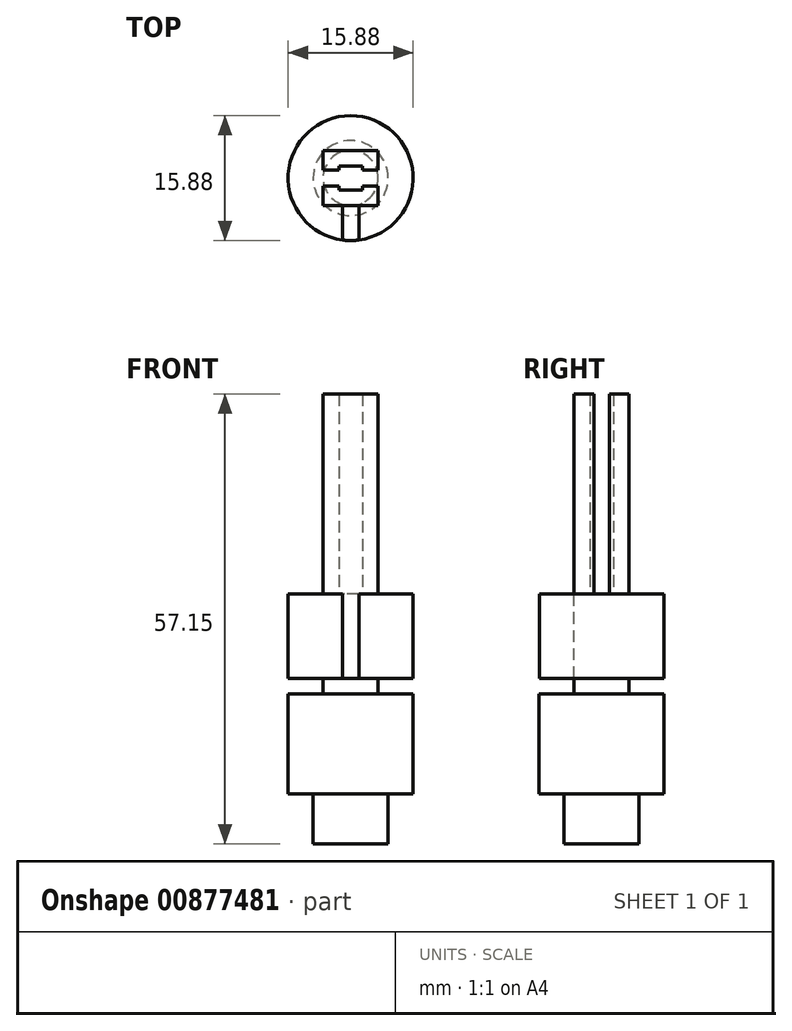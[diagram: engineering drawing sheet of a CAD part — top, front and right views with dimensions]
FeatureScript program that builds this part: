
annotation { "Feature Type Name" : "Feature", "Feature Type Description" : "" }
export const myFeature = defineFeature(function(context is Context, id is Id, definition is map)
    precondition{}
    {
        {
            var Q0;
            Q0=qCreatedBy(makeId("Top.planeOp"),FACE);
            var sketch = newSketch(context, id + "F0", { "sketchPlane" : qUnion([Q0])});
            skCircle(sketch, "E0", {"center": v(0, 0) * mm, "radius": 7.94 * mm});
            skSolve(sketch);
        }
        {
            var Q0;
            Q0 = qSketchRegion(id + "F0", true);
            extrude(context, id + "F1", {"entities" : qUnion([Q0]), "depth" : 25.4 * mm, "offsetDistance" : 25.4 * mm});
        }
        {
            var Q0;
            Q0=qCreatedBy(makeId("Top.planeOp"),FACE);
            var sketch = newSketch(context, id + "F2", { "sketchPlane" : qUnion([Q0])});
            skCircle(sketch, "E1", {"center": v(0, 0) * mm, "radius": 4.76 * mm});
            skSolve(sketch);
        }
        {
            var Q0;
            Q0 = qSketchRegion(id + "F2", true);
            extrude(context, id + "F3", {"entities" : qUnion([Q0]), "operationType" : NewBodyOperationType.ADD, "oppositeDirection" : true, "depth" : 6.35 * mm, "offsetDistance" : 25.4 * mm});
        }
        {
            var Q0;
            Q0=makeQuery(id+"F1.opExtrude","CAP_FACE",FACE,{"disambiguationData":[OSD([sQuery(id+"F0.wireOp",EDGE,"E0")])],"isStart":false});
            var sketch = newSketch(context, id + "F4", { "sketchPlane" : qUnion([Q0])});
            skLineSegment(sketch, "E2.bottom", {"start": v(3.5, 3.5) * mm, "end": v(-3.5, 3.5) * mm});
            skLineSegment(sketch, "E2.top", {"start": v(3.5, -3.5) * mm, "end": v(-3.5, -3.5) * mm});
            skLineSegment(sketch, "E2.left", {"start": v(3.5, 3.5) * mm, "end": v(3.5, -3.5) * mm});
            skLineSegment(sketch, "E2.right", {"start": v(-3.5, 3.5) * mm, "end": v(-3.5, -3.5) * mm});
            skPoint(sketch, "E2.middle", {"position": v(0, 0) * mm});
            skSolve(sketch);
        }
        {
            var Q0;
            Q0 = qSketchRegion(id + "F4", true);
            extrude(context, id + "F5", {"entities" : qUnion([Q0]), "operationType" : NewBodyOperationType.ADD, "depth" : 25.4 * mm, "offsetDistance" : 25.4 * mm});
        }
        {
            var Q0;
            Q0=makeQuery(id+"F1.opExtrude","CAP_FACE",FACE,{"disambiguationData":[OSD([sQuery(id+"F0.wireOp",EDGE,"E0")])],"isStart":false});
            var sketch = newSketch(context, id + "F6", { "sketchPlane" : qUnion([Q0])});
            skLineSegment(sketch, "E3.bottom", {"start": v(1.5, 1.5) * mm, "end": v(-1.5, 1.5) * mm});
            skLineSegment(sketch, "E3.top", {"start": v(1.5, -1.5) * mm, "end": v(-1.5, -1.5) * mm});
            skLineSegment(sketch, "E3.left", {"start": v(1.5, 1.5) * mm, "end": v(1.5, -1.5) * mm});
            skLineSegment(sketch, "E3.right", {"start": v(-1.5, 1.5) * mm, "end": v(-1.5, -1.5) * mm});
            skPoint(sketch, "E3.middle", {"position": v(0, 0) * mm});
            skSolve(sketch);
        }
        {
            var Q0;
            Q0 = qSketchRegion(id + "F6", true);
            extrude(context, id + "F7", {"entities" : qUnion([Q0]), "depth" : 25.4 * mm, "offsetDistance" : 25.4 * mm});
        }
        {
            var Q0;
            Q0=makeQuery(id+"F7.opExtrude","SWEPT_BODY",BODY,{"disambiguationData":[OSD([sQuery(id+"F6.wireOp",EDGE,"E3.bottom"),sQuery(id+"F6.wireOp",EDGE,"E3.top"),sQuery(id+"F6.wireOp",EDGE,"E3.left"),sQuery(id+"F6.wireOp",EDGE,"E3.right")])]});
            var Q1;
            Q1=makeQuery(id+"F1.opExtrude","SWEPT_BODY",BODY,{"disambiguationData":[OSD([sQuery(id+"F0.wireOp",EDGE,"E0")])]});
            booleanBodies(context, id + "F8", {"operationType" : BooleanOperationType.SUBTRACTION, "tools" : qUnion([Q0]), "targets" : qUnion([Q1])});
        }
        {
            var Q0;
            Q0=makeQuery(id+"F1.opExtrude","CAP_FACE",FACE,{"disambiguationData":[OSD([sQuery(id+"F0.wireOp",EDGE,"E0")])],"isStart":false});
            var sketch = newSketch(context, id + "F9", { "sketchPlane" : qUnion([Q0])});
            skLineSegment(sketch, "E4.bottom", {"start": v(7.87, 1) * mm, "end": v(-7.87, 1) * mm});
            skLineSegment(sketch, "E4.top", {"start": v(7.87, -1) * mm, "end": v(-7.87, -1) * mm});
            skLineSegment(sketch, "E4.left", {"start": v(7.87, 1) * mm, "end": v(7.87, -1) * mm});
            skLineSegment(sketch, "E4.right", {"start": v(-7.87, 1) * mm, "end": v(-7.87, -1) * mm});
            skPoint(sketch, "E4.middle", {"position": v(0, 0) * mm});
            skSolve(sketch);
        }
        {
            var Q0;
            Q0 = qSketchRegion(id + "F9", true);
            extrude(context, id + "F10", {"entities" : qUnion([Q0]), "depth" : 25.4 * mm, "offsetDistance" : 25.4 * mm});
        }
        {
            var Q0;
            Q0=makeQuery(id+"F10.opExtrude","SWEPT_BODY",BODY,{"disambiguationData":[OSD([sQuery(id+"F9.wireOp",EDGE,"E4.bottom"),sQuery(id+"F9.wireOp",EDGE,"E4.top"),sQuery(id+"F9.wireOp",EDGE,"E4.left"),sQuery(id+"F9.wireOp",EDGE,"E4.right")])]});
            var Q1;
            Q1=makeQuery(id+"F1.opExtrude","SWEPT_BODY",BODY,{"disambiguationData":[OSD([sQuery(id+"F0.wireOp",EDGE,"E0")])]});
            booleanBodies(context, id + "F11", {"operationType" : BooleanOperationType.SUBTRACTION, "tools" : qUnion([Q0]), "targets" : qUnion([Q1])});
        }
        {
            var Q0;
            Q0=makeQuery(id+"F5.opExtrude","SWEPT_FACE",FACE,{"disambiguationData":[OSD([sQuery(id+"F4.wireOp",EDGE,"E2.top")])]});
            var sketch = newSketch(context, id + "F12", { "sketchPlane" : qUnion([Q0])});
            skLineSegment(sketch, "E5.bottom", {"start": v(1.04, 12.7) * mm, "end": v(-1.04, 12.7) * mm});
            skLineSegment(sketch, "E5.top", {"start": v(1.04, 25.4) * mm, "end": v(-1.04, 25.4) * mm});
            skLineSegment(sketch, "E5.left", {"start": v(1.04, 12.7) * mm, "end": v(1.04, 25.4) * mm});
            skLineSegment(sketch, "E5.right", {"start": v(-1.04, 12.7) * mm, "end": v(-1.04, 25.4) * mm});
            skPoint(sketch, "E5.middle", {"position": v(0, 19.05) * mm});
            skSolve(sketch);
        }
        {
            var Q0;
            Q0 = qSketchRegion(id + "F12", true);
            extrude(context, id + "F13", {"entities" : qUnion([Q0]), "depth" : 25.4 * mm, "offsetDistance" : 25.4 * mm});
        }
        {
            var Q0;
            Q0=makeQuery(id+"F13.opExtrude","SWEPT_BODY",BODY,{"disambiguationData":[OSD([sQuery(id+"F12.wireOp",EDGE,"E5.bottom"),sQuery(id+"F12.wireOp",EDGE,"E5.top"),sQuery(id+"F12.wireOp",EDGE,"E5.left"),sQuery(id+"F12.wireOp",EDGE,"E5.right")])]});
            var Q1;
            Q1=makeQuery(id+"F1.opExtrude","SWEPT_BODY",BODY,{"disambiguationData":[OSD([sQuery(id+"F0.wireOp",EDGE,"E0")])]});
            booleanBodies(context, id + "F14", {"operationType" : BooleanOperationType.SUBTRACTION, "tools" : qUnion([Q0]), "targets" : qUnion([Q1])});
        }
        {
            var Q0;
            Q0=makeQuery(id+"F14.opBoolean","COPY",FACE,{"derivedFrom":makeQuery(id+"F13.opExtrude","SWEPT_FACE",FACE,{"disambiguationData":[OSD([sQuery(id+"F12.wireOp",EDGE,"E5.bottom")])]})});
            var sketch = newSketch(context, id + "F15", { "sketchPlane" : qUnion([Q0])});
            skCircle(sketch, "E6", {"center": v(0, 0) * mm, "radius": 3.5 * mm});
            skCircle(sketch, "E7", {"center": v(0, 0) * mm, "radius": 7.94 * mm});
            skSolve(sketch);
        }
        {
            var Q0;
            Q0 = qSketchRegion(id + "F15", true);
            extrude(context, id + "F16", {"entities" : qUnion([Q0]), "depth" : 2 * mm, "offsetDistance" : 25.4 * mm});
        }
        {
            var Q0;
            Q0=makeQuery(id+"F16.opExtrude","SWEPT_BODY",BODY,{"disambiguationData":[OSD([sQuery(id+"F15.wireOp",EDGE,"E6"),sQuery(id+"F15.wireOp",EDGE,"E7")])]});
            var Q1;
            Q1=makeQuery(id+"F1.opExtrude","SWEPT_BODY",BODY,{"disambiguationData":[OSD([sQuery(id+"F0.wireOp",EDGE,"E0")])]});
            booleanBodies(context, id + "F17", {"operationType" : BooleanOperationType.SUBTRACTION, "tools" : qUnion([Q0]), "targets" : qUnion([Q1])});
        }
    });
